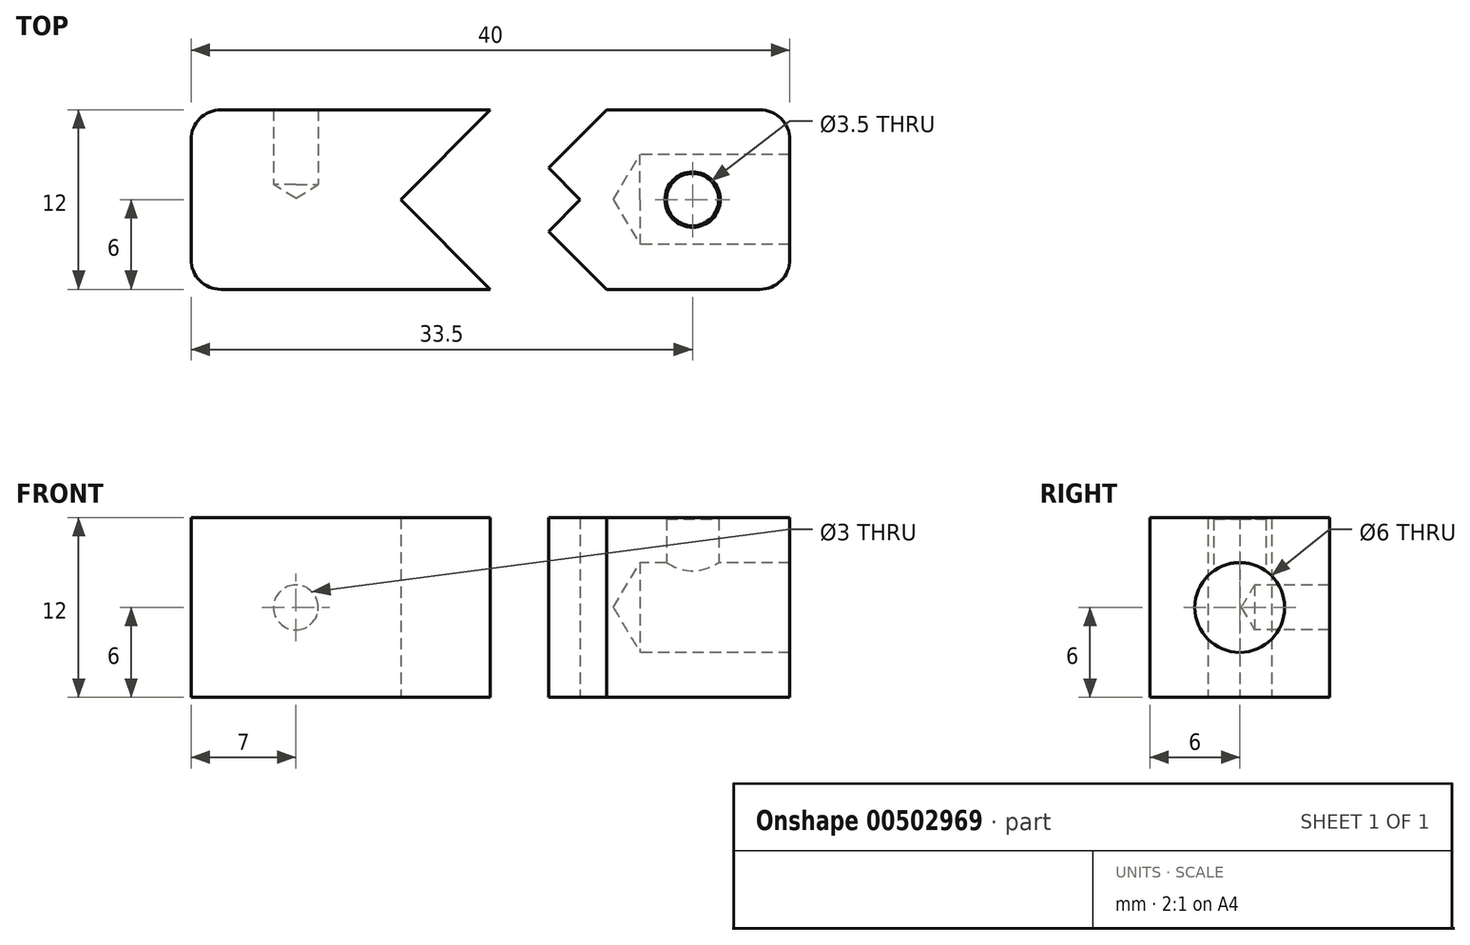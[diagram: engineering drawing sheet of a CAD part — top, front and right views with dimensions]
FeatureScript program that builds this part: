
annotation { "Feature Type Name" : "Feature", "Feature Type Description" : "" }
export const myFeature = defineFeature(function(context is Context, id is Id, definition is map)
    precondition{}
    {
        {
            var Q0;
            Q0=qCreatedBy(makeId("Top.planeOp"),FACE);
            var sketch = newSketch(context, id + "F0", { "sketchPlane" : qUnion([Q0])});
            skLineSegment(sketch, "E0.bottom", {"start": v(-20, 6) * mm, "end": v(20, 6) * mm});
            skLineSegment(sketch, "E0.top", {"start": v(-20, -6) * mm, "end": v(20, -6) * mm});
            skLineSegment(sketch, "E0.left", {"start": v(-20, 6) * mm, "end": v(-20, -6) * mm});
            skLineSegment(sketch, "E0.right", {"start": v(20, 6) * mm, "end": v(20, -6) * mm});
            skLineSegment(sketch, "E1", {"start": v(0, 6) * mm, "end": v(-6, 0) * mm});
            skLineSegment(sketch, "E2", {"start": v(-6, 0) * mm, "end": v(0, -6) * mm});
            skLineSegment(sketch, "E3.MirrorCS", {"start": v(0, 6) * mm, "end": v(6, 0) * mm});
            skLineSegment(sketch, "E4.MirrorCS", {"start": v(6, 0) * mm, "end": v(0, -6) * mm});
            skLineSegment(sketch, "E5", {"start": v(-6, 0) * mm, "end": v(-3.88, 2.12) * mm});
            skLineSegment(sketch, "E6", {"start": v(-3.88, 2.12) * mm, "end": v(-1.76, 0) * mm});
            skLineSegment(sketch, "E7", {"start": v(-1.76, 0) * mm, "end": v(-3.88, -2.12) * mm});
            skLineSegment(sketch, "E8", {"start": v(3.88, 2.12) * mm, "end": v(7.76, 6) * mm});
            skLineSegment(sketch, "E9", {"start": v(3.88, -2.12) * mm, "end": v(7.76, -6) * mm});
            skSolve(sketch);
        }
        {
            var Q0;
            {var subQ0=sQuery(id+"F0.wireOp",EDGE,"E0.left");Q0=makeQuery(id+"F0.imprint","IMPRINT",FACE,{"disambiguationData":[TD([[makeQuery(id+"F0.imprint","IMPRINT",EDGE,{"derivedFrom":subQ0}),1.0]])]});}
            extrude(context, id + "F1", {"entities" : qUnion([Q0]), "depth" : 12 * mm, "offsetDistance" : 25 * mm, "symmetric" : true});
        }
        {
            var Q0;
            {var subQ0=sQuery(id+"F0.wireOp",EDGE,"E0.right");Q0=makeQuery(id+"F0.imprint","IMPRINT",FACE,{"disambiguationData":[TD([[makeQuery(id+"F0.imprint","IMPRINT",EDGE,{"derivedFrom":subQ0}),-1.0]])]});}
            extrude(context, id + "F2", {"entities" : qUnion([Q0]), "depth" : 12 * mm, "offsetDistance" : 25 * mm, "symmetric" : true});
        }
        {
            var Q0;
            Q0=makeQuery(id+"F2.opExtrude","SWEPT_FACE",FACE,{"disambiguationData":[OSD([sQuery(id+"F0.wireOp",EDGE,"E0.right")])]});
            var sketch = newSketch(context, id + "F3", { "sketchPlane" : qUnion([Q0])});
            skPoint(sketch, "E10", {"position": v(0, 0) * mm});
            skSolve(sketch);
        }
        {
            var Q0;
            Q0=sQuery(id+"F3.wireOp",VERTEX,"E10");
            var Q1;
            Q1=makeQuery(id+"F2.opExtrude","SWEPT_BODY",BODY,{"disambiguationData":[OSD([sQuery(id+"F0.wireOp",EDGE,"E0.bottom"),sQuery(id+"F0.wireOp",EDGE,"E0.top"),sQuery(id+"F0.wireOp",EDGE,"E0.right"),sQuery(id+"F0.wireOp",EDGE,"E3.MirrorCS"),sQuery(id+"F0.wireOp",EDGE,"E4.MirrorCS"),sQuery(id+"F0.wireOp",EDGE,"E8"),sQuery(id+"F0.wireOp",EDGE,"E9")])]});
            hole(context, id + "F4", {"style" : HoleStyle.SIMPLE, "endStyle" : HoleEndStyle.BLIND, "standardTappedOrClearance" : lookupTablePath({ "standard" : "ISO", "size" : "6", "type" : "Drilled" }), "standardBlindInLast" : lookupTablePath({ "standard" : "ISO", "size" : "6", "type" : "Drilled" }), "holeDiameter" : 6 * mm, "holeDepth" : 10 * mm, "isTappedThrough" : true, "tappedDepth" : 12.7 * mm, "tapClearance" : 3, "locations" : qUnion([Q0]), "scope" : qUnion([Q1]), "startStyle" : HoleStartStyle.PART});
        }
        {
            var Q0;
            Q0=makeQuery(id+"F2.opExtrude","CAP_FACE",FACE,{"disambiguationData":[OSD([sQuery(id+"F0.wireOp",EDGE,"E0.bottom"),sQuery(id+"F0.wireOp",EDGE,"E0.top"),sQuery(id+"F0.wireOp",EDGE,"E0.right"),sQuery(id+"F0.wireOp",EDGE,"E3.MirrorCS"),sQuery(id+"F0.wireOp",EDGE,"E4.MirrorCS"),sQuery(id+"F0.wireOp",EDGE,"E8"),sQuery(id+"F0.wireOp",EDGE,"E9")])],"isStart":false});
            var sketch = newSketch(context, id + "F5", { "sketchPlane" : qUnion([Q0])});
            skPoint(sketch, "E11", {"position": v(13.5, 0) * mm});
            skSolve(sketch);
        }
        {
            var Q0;
            Q0=sQuery(id+"F5.wireOp",VERTEX,"E11");
            var Q1;
            Q1=makeQuery(id+"F2.opExtrude","SWEPT_BODY",BODY,{"disambiguationData":[OSD([sQuery(id+"F0.wireOp",EDGE,"E0.bottom"),sQuery(id+"F0.wireOp",EDGE,"E0.top"),sQuery(id+"F0.wireOp",EDGE,"E0.right"),sQuery(id+"F0.wireOp",EDGE,"E3.MirrorCS"),sQuery(id+"F0.wireOp",EDGE,"E4.MirrorCS"),sQuery(id+"F0.wireOp",EDGE,"E8"),sQuery(id+"F0.wireOp",EDGE,"E9")])]});
            hole(context, id + "F6", {"style" : HoleStyle.C_SINK, "endStyle" : HoleEndStyle.BLIND, "holeDiameter" : 3.5 * mm, "cSinkDiameter" : 3.7 * mm, "cSinkAngle" : 90 * degree, "holeDepth" : 6.5 * mm, "isTappedThrough" : true, "tappedDepth" : 5 * mm, "tapClearance" : 3, "locations" : qUnion([Q0]), "scope" : qUnion([Q1]), "startStyle" : HoleStartStyle.PART});
        }
        {
            var Q0;
            Q0=makeQuery(id+"F1.opExtrude","SWEPT_FACE",FACE,{"disambiguationData":[OSD([sQuery(id+"F0.wireOp",EDGE,"E0.bottom")])]});
            var sketch = newSketch(context, id + "F7", { "sketchPlane" : qUnion([Q0])});
            skPoint(sketch, "E12", {"position": v(13, 0) * mm});
            skPoint(sketch, "E12.positionSnap0", {"position": v(20, 0) * mm});
            skSolve(sketch);
        }
        {
            var Q0;
            Q0=sQuery(id+"F7.wireOp",VERTEX,"E12");
            var Q1;
            Q1=makeQuery(id+"F1.opExtrude","SWEPT_BODY",BODY,{"disambiguationData":[OSD([sQuery(id+"F0.wireOp",EDGE,"E0.bottom"),sQuery(id+"F0.wireOp",EDGE,"E0.top"),sQuery(id+"F0.wireOp",EDGE,"E0.left"),sQuery(id+"F0.wireOp",EDGE,"E1"),sQuery(id+"F0.wireOp",EDGE,"E2"),sQuery(id+"F0.wireOp",EDGE,"E5")])]});
            hole(context, id + "F8", {"style" : HoleStyle.SIMPLE, "endStyle" : HoleEndStyle.BLIND, "holeDiameter" : 3 * mm, "holeDepth" : 5 * mm, "isTappedThrough" : true, "tappedDepth" : 5 * mm, "tapClearance" : 3, "locations" : qUnion([Q0]), "scope" : qUnion([Q1]), "startStyle" : HoleStartStyle.PART});
        }
        {
            var Q0;
            Q0=makeQuery(id+"F2.opExtrude","SWEPT_EDGE",EDGE,{"disambiguationData":[OSD([sQuery(id+"F0.wireOp",EDGE,"E0.bottom"),sQuery(id+"F0.wireOp",EDGE,"E0.right")])]});
            var Q1;
            Q1=makeQuery(id+"F2.opExtrude","SWEPT_EDGE",EDGE,{"disambiguationData":[OSD([sQuery(id+"F0.wireOp",EDGE,"E0.top"),sQuery(id+"F0.wireOp",EDGE,"E0.right")])]});
            var Q2;
            Q2=makeQuery(id+"F1.opExtrude","SWEPT_EDGE",EDGE,{"disambiguationData":[OSD([sQuery(id+"F0.wireOp",EDGE,"E0.bottom"),sQuery(id+"F0.wireOp",EDGE,"E0.left")])]});
            var Q3;
            Q3=makeQuery(id+"F1.opExtrude","SWEPT_EDGE",EDGE,{"disambiguationData":[OSD([sQuery(id+"F0.wireOp",EDGE,"E0.top"),sQuery(id+"F0.wireOp",EDGE,"E0.left")])]});
            fillet(context, id + "F9", {"entities" : qUnion([Q0, Q1, Q2, Q3]), "radius" : 2 * mm, "tangentPropagation" : true, "allowEdgeOverflow" : false});
        }
    });
